# Revit family: REVIT-MG-1029-Haander---
name_source: partatom
category: Furniture
revit_build: Autodesk Revit 2016 (Build: 20150220_1215(x64)
units: mm (PartAtom-declared; Revit-internal decimal feet)

## family parameters
Always vertical = Yes
Cut with Voids When Loaded = No
OmniClass Number = 23.40.20.00
OmniClass Title = General Furniture and Specialties
Room Calculation Point = No
Shared = No
Work Plane-Based = No

## types (1)
- MG-1029
    Description = Haander Freestanding
    Low Emitting Finish = Yes
    Low Emitting Material = Yes
    Manufacturer = Magnuson Group
    Miscellaneous Finish = MAG - Plastic White
    Model = MG-1029
    PPE Station = Yes
    Percentage of Recycled Content = 0
    Revit File Built By = https://servex-us.com
    Salvage or Reuse = Yes
    Tray Finish = MAG - Metalic Anodized Bronze
    Type Comments = Huddle Rooms
    URL = www.magnusongroup.com

## geometry (parser evidence)
native form markers: Blend x2, Sweep x6
no freeform markers — native parametric forms only
